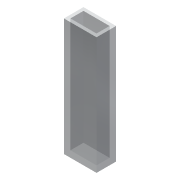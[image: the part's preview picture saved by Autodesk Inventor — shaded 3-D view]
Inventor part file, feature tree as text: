
AUTODESK INVENTOR PART (.ipt)
format: ipt  version: 2021 (Build 250183000, 183)  size: 87,552 bytes
history: native  units: mm
features: extrude x2, sketch x2
ambient origin geometry x8: Origin, YZ Plane, XZ Plane, XY Plane, X Axis, Y Axis, Z Axis, Center Point
bodies: Solid1 (feature_tree)
feature tree (4):
  extrude  "Extrusion1"  Depth=12.5mm
  extrude  "Extrusion2"  Depth=10.0mm
  sketch  "Sketch1"  dims[d0=7.5mm d1=12.5mm]
  sketch  "Sketch2"  dims[d2=45.0mm d3=0.0mm d4=10.0mm d5=5.0mm d6=1.25mm d7=1.25mm d8=43.75mm d9=0.0mm]
